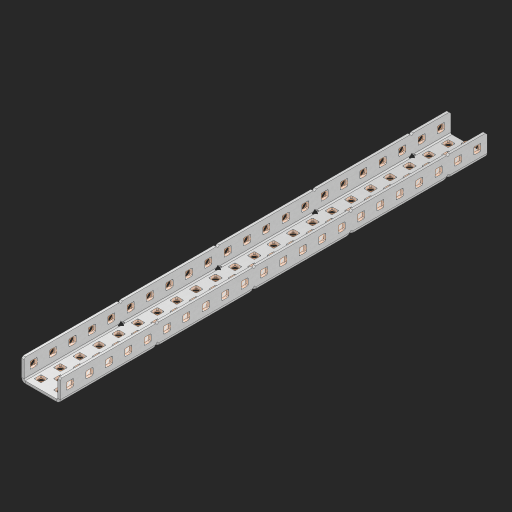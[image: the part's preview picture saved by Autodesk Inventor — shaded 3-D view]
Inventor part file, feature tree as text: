
AUTODESK INVENTOR PART (.ipt)
format: ipt  version: 2023 (Build 270158000, 158)  size: 1,501,696 bytes
history: native  units: in
note: dims shown in document units (in); Inventor stores cm internally (conversion verified against a paired STEP export)
features: other x117, extrude x108, sheet_metal_op x11, sketch x10, pattern_linear x2, mirror x1, chamfer x1
ambient origin geometry x8: Origin, YZ Plane, XZ Plane, XY Plane, X Axis, Y Axis, Z Axis, Center Point
bodies: Solid1 (feature_tree), Body (feature_tree)
feature tree (250):
  sheet_metal_op  "Flanges"
  other  "Flange Pattern Plane"
  other  "Flange Pattern Sketch"
  sheet_metal_op  "Flange Pattern"
  sheet_metal_op  "Body Pattern"
  pattern_linear  "Center Pattern"  Spacing1=0.0625in  [1 undecoded]
  other  "Arc Length"
  mirror  "Notch Mirror"
  pattern_linear  "Notch Pattern"  Spacing1=0.182in  [1 undecoded]
  chamfer  "End Chamfer"
  extrude  "Half Cut"  Depth=0.02in
  sketch  "Sketch1"  dims[d0=1.0in]
  other  "Plate1"
  sketch  "Sketch2"  dims[d1=11.0in]
  other  "Plate2"
  sheet_metal_op  "Bend1"
  sheet_metal_op  "Corner1"
  sketch  "Sketch3"  dims[d2=0.0625in]
  sketch  "Sketch7"  dims[d3=0.0625in]
  other  "Srf1"
  other  "Srf2"
  sketch  "Sketch8"  dims[d4=0.0312in]
  sketch  "Sketch9"  dims[d5=0.125in]
  other  "Srf91"
  sheet_metal_op  "Body Pattern Sketch"
  other  "Srf92"
  sketch  "Sketch13"  dims[d6=0.0625in]
  sketch  "Sketch14"  dims[d7=0.5in d8=90.0deg d9=0.0312in]
  sketch  "Sketch15"  dims[d10=0.25in]
  sketch  "Sketch16"  dims[d11=0.0625in d12=0.0625in d16=0.182in d17=0.02in d18=0.0625in d19=0.0in d20=0.25in d21=0.25in d38=8.6614in d40=0.5in d41=0.7874in d43=1.0in d46=0.172in d47=1.0in d48=0.0in d49=0.182in d50=0.02in d51=0.25in d52=0.25in d53=0.0625in d54=0.0in d55=0.172in d56=1.0in d57=0.0in d58=0.25in d60=8.6614in d62=0.5in d63=0.7874in d65=0.5in d85=0.1473in d86=0.1782in d88=0.04in d89=0.0625in d90=0.0in d91=0.04in d92=0.0491in d95=2.5in d96=0.04in d97=0.25in d98=45.0deg d99=0.25in d100=0.5in d101=0.0in d102=2.497in d106=0.182in d107=0.02in d108=0.5in d109=0.5in d110=0.0625in d111=0.0in d112=0.172in d113=0.5in d114=0.0in d117=0.5in d118=0.5in d119=0.5in]
  other  "Srf786"
  other  "Srf823"
  other  "Srf824"
  other  "Srf825"
  other  "Srf826"
  other  "Srf827"
  other  "Srf828"
  other  "Srf829"
  other  "Srf856"
  other  "Srf857"
  other  "Srf858"
  other  "Srf859"
  other  "Srf860"
  other  "Srf861"
  other  "Srf862"
  other  "Srf889"
  other  "Srf890"
  other  "Srf891"
  other  "Srf892"
  other  "Srf893"
  other  "Srf894"
  other  "Srf895"
  other  "Srf896"
  other  "Srf922"
  other  "Srf923"
  other  "Srf924"
  other  "Srf925"
  other  "Srf926"
  other  "Srf959"
  other  "Srf960"
  other  "Srf961"
  other  "Srf962"
  other  "Srf963"
  other  "Srf996"
  other  "Srf997"
  other  "Srf998"
  other  "Srf999"
  other  "Srf1000"
  other  "Srf1143"
  other  "Srf1144"
  other  "Srf1145"
  other  "Srf1146"
  other  "Srf1147"
  other  "Srf1148"
  other  "Srf1149"
  other  "Srf1150"
  other  "Srf1151"
  other  "Srf1152"
  other  "Srf1153"
  other  "Srf1154"
  other  "Srf1155"
  other  "Srf1156"
  other  "Srf1157"
  other  "Srf1158"
  other  "Srf1159"
  other  "Srf1160"
  other  "Srf1161"
  other  "Srf1162"
  other  "Srf1163"
  other  "Srf1164"
  other  "Srf1165"
  other  "Srf1166"
  other  "Srf1167"
  other  "Srf1168"
  other  "Srf1169"
  other  "Srf1170"
  other  "Srf1171"
  other  "Srf1172"
  other  "Srf1199"
  other  "Srf1200"
  other  "Srf1201"
  other  "Srf1202"
  other  "Srf1203"
  other  "Srf1204"
  other  "Srf1205"
  other  "Srf1206"
  other  "Srf1207"
  other  "Srf1208"
  other  "Srf1209"
  other  "Srf1210"
  other  "Srf1211"
  other  "Srf1212"
  other  "Srf1213"
  other  "Srf1214"
  other  "Srf1215"
  other  "Srf1216"
  other  "Srf1217"
  other  "Srf1218"
  other  "Srf1219"
  other  "Srf1220"
  other  "Srf1221"
  other  "Srf1222"
  other  "Srf1223"
  other  "Srf1224"
  other  "Srf1225"
  other  "Srf1226"
  other  "Srf1227"
  other  "Srf1228"
  other  "Srf1255"
  other  "Srf1256"
  other  "Srf1257"
  other  "Srf1258"
  other  "Srf1259"
  other  "Srf1260"
  other  "Srf1261"
  other  "Srf1262"
  sheet_metal_op  "Flange Stamp"
  sheet_metal_op  "Flange Circle"
  sheet_metal_op  "Body Stamp"
  sheet_metal_op  "Body Circle"
  other  "Center Stamp"
  other  "Center Circle"
  sheet_metal_op  "Notch"
  extrude  "ExtrusionSrf2"  Depth=0.0625in
  extrude  "ExtrusionSrf92"  TaperAngle=0.0deg  [1 undecoded]
  extrude  "ExtrusionSrf823"  Depth=0.5in
  extrude  "ExtrusionSrf824"  Depth=0.5in
  extrude  "ExtrusionSrf825"  Depth=0.5in
  extrude  "ExtrusionSrf826"  Depth=0.5in
  extrude  "ExtrusionSrf827"  Depth=1.0in TaperAngle=0.0deg
  extrude  "ExtrusionSrf828"  Depth=0.5in
  extrude  "ExtrusionSrf829"  Depth=0.02in
  extrude  "ExtrusionSrf856"  Depth=0.5in
  extrude  "ExtrusionSrf857"  Depth=0.5in
  extrude  "ExtrusionSrf858"  Depth=0.0625in
  extrude  "ExtrusionSrf859"  TaperAngle=0.0deg  [1 undecoded]
  extrude  "ExtrusionSrf860"  Depth=0.5in
  extrude  "ExtrusionSrf861"  Depth=1.0in TaperAngle=0.0deg
  extrude  "ExtrusionSrf862"  Depth=0.5in
  extrude  "ExtrusionSrf889"  Depth=0.5in
  extrude  "ExtrusionSrf890"  Depth=0.5in
  extrude  "ExtrusionSrf891"  Depth=0.5in
  extrude  "ExtrusionSrf892"  Depth=0.5in
  extrude  "ExtrusionSrf893"  Depth=0.5in
  extrude  "ExtrusionSrf894"  Depth=0.0625in
  extrude  "ExtrusionSrf895"  TaperAngle=0.0deg  [1 undecoded]
  extrude  "ExtrusionSrf896"  Depth=0.5in
  extrude  "ExtrusionSrf922"  Depth=0.5in
  extrude  "ExtrusionSrf923"  Depth=2.5in
  extrude  "ExtrusionSrf924"  Depth=0.5in TaperAngle=45.0deg
  extrude  "ExtrusionSrf925"  Depth=0.5in
  extrude  "ExtrusionSrf926"  Depth=0.5in TaperAngle=0.0deg
  extrude  "ExtrusionSrf959"  Depth=0.5in
  extrude  "ExtrusionSrf960"  Depth=0.5in
  extrude  "ExtrusionSrf961"  Depth=0.02in
  extrude  "ExtrusionSrf962"  Depth=0.5in
  extrude  "ExtrusionSrf963"  Depth=0.5in
  extrude  "ExtrusionSrf996"  Depth=0.0625in
  extrude  "ExtrusionSrf997"  TaperAngle=0.0deg  [1 undecoded]
  extrude  "ExtrusionSrf998"  Depth=0.5in
  extrude  "ExtrusionSrf999"  Depth=0.5in TaperAngle=0.0deg
  extrude  "ExtrusionSrf1000"  Depth=0.5in
  extrude  "ExtrusionSrf1143"  Depth=0.5in
  extrude  "ExtrusionSrf1144"  Depth=0.5in
  extrude  "ExtrusionSrf1145"  [1 undecoded]
  extrude  "ExtrusionSrf1146"  [1 undecoded]
  extrude  "ExtrusionSrf1147"  [1 undecoded]
  extrude  "ExtrusionSrf1148"  [1 undecoded]
  extrude  "ExtrusionSrf1149"  [1 undecoded]
  extrude  "ExtrusionSrf1150"  [1 undecoded]
  extrude  "ExtrusionSrf1151"  [1 undecoded]
  extrude  "ExtrusionSrf1152"  [1 undecoded]
  extrude  "ExtrusionSrf1153"  [1 undecoded]
  extrude  "ExtrusionSrf1154"  [1 undecoded]
  extrude  "ExtrusionSrf1155"  [1 undecoded]
  extrude  "ExtrusionSrf1156"  [1 undecoded]
  extrude  "ExtrusionSrf1157"  [1 undecoded]
  extrude  "ExtrusionSrf1158"  [1 undecoded]
  extrude  "ExtrusionSrf1159"  [1 undecoded]
  extrude  "ExtrusionSrf1160"  [1 undecoded]
  extrude  "ExtrusionSrf1161"  [1 undecoded]
  extrude  "ExtrusionSrf1162"  [1 undecoded]
  extrude  "ExtrusionSrf1163"  [1 undecoded]
  extrude  "ExtrusionSrf1164"  [1 undecoded]
  extrude  "ExtrusionSrf1165"  [1 undecoded]
  extrude  "ExtrusionSrf1166"  [1 undecoded]
  extrude  "ExtrusionSrf1167"  [1 undecoded]
  extrude  "ExtrusionSrf1168"  [1 undecoded]
  extrude  "ExtrusionSrf1169"  [1 undecoded]
  extrude  "ExtrusionSrf1170"  [1 undecoded]
  extrude  "ExtrusionSrf1171"  [1 undecoded]
  extrude  "ExtrusionSrf1172"  [1 undecoded]
  extrude  "ExtrusionSrf1199"  [1 undecoded]
  extrude  "ExtrusionSrf1200"  [1 undecoded]
  extrude  "ExtrusionSrf1201"  [1 undecoded]
  extrude  "ExtrusionSrf1202"  [1 undecoded]
  extrude  "ExtrusionSrf1203"  [1 undecoded]
  extrude  "ExtrusionSrf1204"  [1 undecoded]
  extrude  "ExtrusionSrf1205"  [1 undecoded]
  extrude  "ExtrusionSrf1206"  [1 undecoded]
  extrude  "ExtrusionSrf1207"  [1 undecoded]
  extrude  "ExtrusionSrf1208"  [1 undecoded]
  extrude  "ExtrusionSrf1209"  [1 undecoded]
  extrude  "ExtrusionSrf1210"  [1 undecoded]
  extrude  "ExtrusionSrf1211"  [1 undecoded]
  extrude  "ExtrusionSrf1212"  [1 undecoded]
  extrude  "ExtrusionSrf1213"  [1 undecoded]
  extrude  "ExtrusionSrf1214"  [1 undecoded]
  extrude  "ExtrusionSrf1215"  [1 undecoded]
  extrude  "ExtrusionSrf1216"  [1 undecoded]
  extrude  "ExtrusionSrf1217"  [1 undecoded]
  extrude  "ExtrusionSrf1218"  [1 undecoded]
  extrude  "ExtrusionSrf1219"  [1 undecoded]
  extrude  "ExtrusionSrf1220"  [1 undecoded]
  extrude  "ExtrusionSrf1221"  [1 undecoded]
  extrude  "ExtrusionSrf1222"  [1 undecoded]
  extrude  "ExtrusionSrf1223"  [1 undecoded]
  extrude  "ExtrusionSrf1224"  [1 undecoded]
  extrude  "ExtrusionSrf1225"  [1 undecoded]
  extrude  "ExtrusionSrf1226"  [1 undecoded]
  extrude  "ExtrusionSrf1227"  [1 undecoded]
  extrude  "ExtrusionSrf1228"  [1 undecoded]
  extrude  "ExtrusionSrf1255"  [1 undecoded]
  extrude  "ExtrusionSrf1256"  [1 undecoded]
  extrude  "ExtrusionSrf1257"  [1 undecoded]
  extrude  "ExtrusionSrf1258"  [1 undecoded]
  extrude  "ExtrusionSrf1259"  [1 undecoded]
  extrude  "ExtrusionSrf1260"  [1 undecoded]
  extrude  "ExtrusionSrf1261"  [1 undecoded]
  extrude  "ExtrusionSrf1262"  [1 undecoded]
note: 72 required parameter values undecoded (feature->parameter linkage not recoverable at this tier; creation-order binding heuristic only, values carry confidence <= 0.55)
